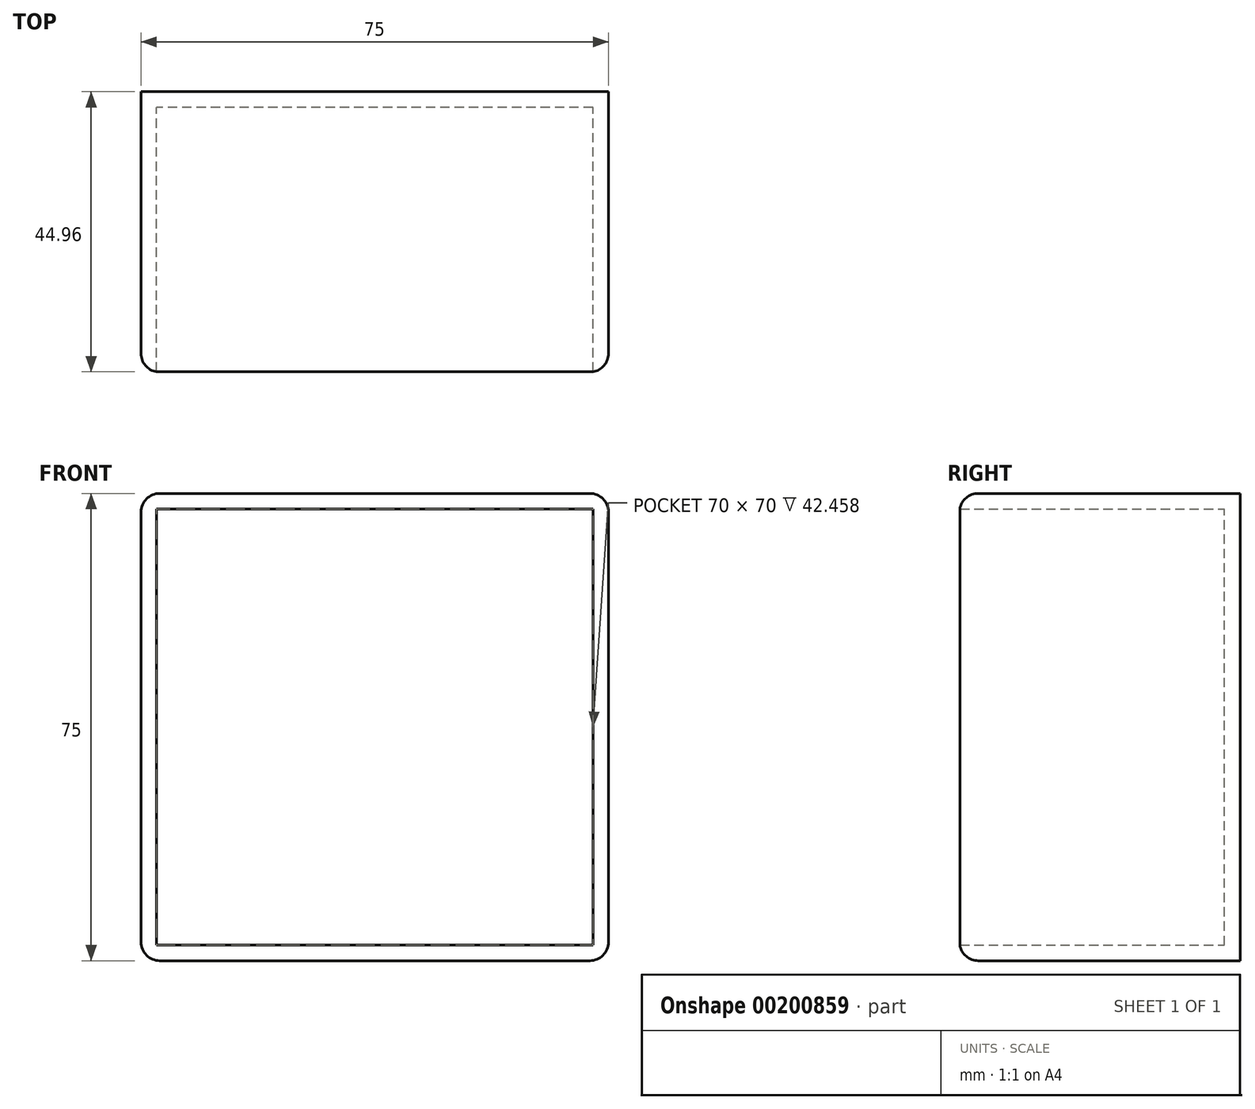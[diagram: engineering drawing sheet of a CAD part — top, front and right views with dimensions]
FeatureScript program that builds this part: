
annotation { "Feature Type Name" : "Feature", "Feature Type Description" : "" }
export const myFeature = defineFeature(function(context is Context, id is Id, definition is map)
    precondition{}
    {
        {
            var Q0;
            Q0=qCreatedBy(makeId("Front.planeOp"),FACE);
            var sketch = newSketch(context, id + "F0", { "sketchPlane" : qUnion([Q0])});
            skLineSegment(sketch, "E0.bottom", {"start": v(37.5, -37.5) * mm, "end": v(-37.5, -37.5) * mm});
            skLineSegment(sketch, "E0.top", {"start": v(37.5, 37.5) * mm, "end": v(-37.5, 37.5) * mm});
            skLineSegment(sketch, "E0.left", {"start": v(37.5, -37.5) * mm, "end": v(37.5, 37.5) * mm});
            skLineSegment(sketch, "E0.right", {"start": v(-37.5, -37.5) * mm, "end": v(-37.5, 37.5) * mm});
            skPoint(sketch, "E0.middle", {"position": v(0, 0) * mm});
            skSolve(sketch);
        }
        {
            var Q0;
            Q0 = qSketchRegion(id + "F0", true);
            extrude(context, id + "F1", {"entities" : qUnion([Q0]), "depth" : 45 * mm, "offsetDistance" : 25 * mm});
        }
        {
            var Q0;
            Q0=makeQuery(id+"F1.opExtrude","CAP_FACE",FACE,{"disambiguationData":[OSD([sQuery(id+"F0.wireOp",EDGE,"E0.bottom"),sQuery(id+"F0.wireOp",EDGE,"E0.top"),sQuery(id+"F0.wireOp",EDGE,"E0.left"),sQuery(id+"F0.wireOp",EDGE,"E0.right")])],"isStart":false});
            shell(context, id + "F2", {"entities" : qUnion([Q0]), "thickness" : 2.5 * mm});
        }
        {
            var Q0;
            Q0=makeQuery(id+"F1.opExtrude","CAP_EDGE",EDGE,{"disambiguationData":[OSD([sQuery(id+"F0.wireOp",EDGE,"E0.right")])],"isStart":false});
            var Q1;
            Q1=makeQuery(id+"F1.opExtrude","CAP_EDGE",EDGE,{"disambiguationData":[OSD([sQuery(id+"F0.wireOp",EDGE,"E0.top")])],"isStart":false});
            var Q2;
            Q2=makeQuery(id+"F1.opExtrude","CAP_EDGE",EDGE,{"disambiguationData":[OSD([sQuery(id+"F0.wireOp",EDGE,"E0.left")])],"isStart":false});
            var Q3;
            Q3=makeQuery(id+"F1.opExtrude","CAP_EDGE",EDGE,{"disambiguationData":[OSD([sQuery(id+"F0.wireOp",EDGE,"E0.bottom")])],"isStart":false});
            fillet(context, id + "F3", {"entities" : qUnion([Q0, Q1, Q2, Q3]), "radius" : 3 * mm, "tangentPropagation" : true, "allowEdgeOverflow" : false});
        }
        {
            var Q0;
            Q0=makeQuery(id+"F1.opExtrude","SWEPT_EDGE",EDGE,{"disambiguationData":[OSD([sQuery(id+"F0.wireOp",EDGE,"E0.top"),sQuery(id+"F0.wireOp",EDGE,"E0.right")])]});
            var Q1;
            Q1=makeQuery(id+"F1.opExtrude","SWEPT_EDGE",EDGE,{"disambiguationData":[OSD([sQuery(id+"F0.wireOp",EDGE,"E0.bottom"),sQuery(id+"F0.wireOp",EDGE,"E0.right")])]});
            var Q2;
            Q2=makeQuery(id+"F1.opExtrude","SWEPT_EDGE",EDGE,{"disambiguationData":[OSD([sQuery(id+"F0.wireOp",EDGE,"E0.bottom"),sQuery(id+"F0.wireOp",EDGE,"E0.left")])]});
            var Q3;
            Q3=makeQuery(id+"F1.opExtrude","SWEPT_EDGE",EDGE,{"disambiguationData":[OSD([sQuery(id+"F0.wireOp",EDGE,"E0.top"),sQuery(id+"F0.wireOp",EDGE,"E0.left")])]});
            fillet(context, id + "F4", {"entities" : qUnion([Q0, Q1, Q2, Q3]), "radius" : 3 * mm, "tangentPropagation" : true, "allowEdgeOverflow" : false});
        }
    });
